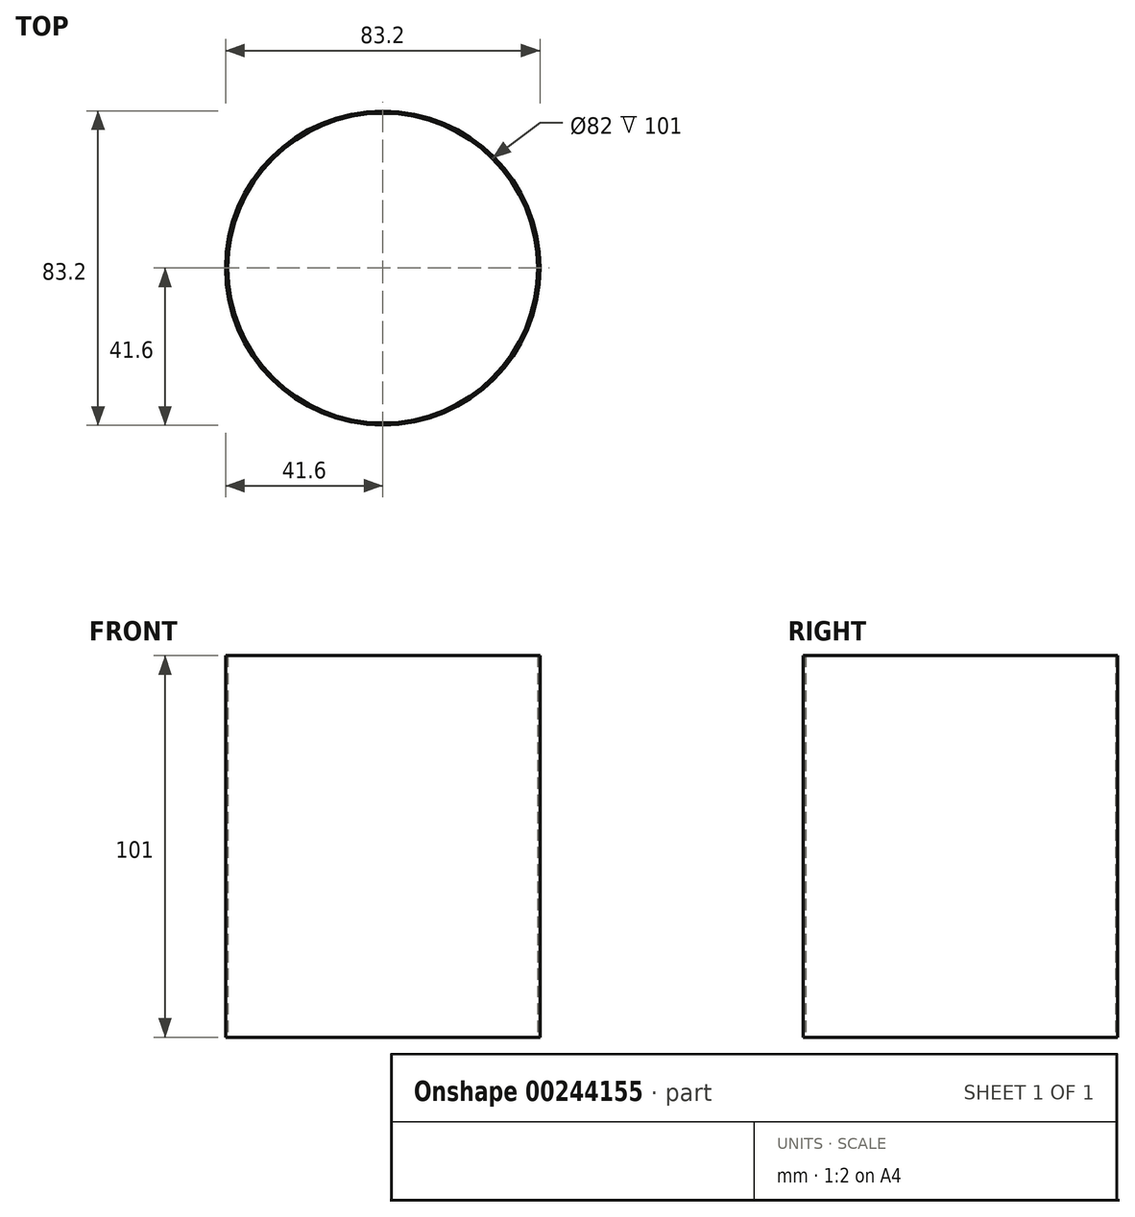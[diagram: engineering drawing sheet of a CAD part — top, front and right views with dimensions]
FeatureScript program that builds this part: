
annotation { "Feature Type Name" : "Feature", "Feature Type Description" : "" }
export const myFeature = defineFeature(function(context is Context, id is Id, definition is map)
    precondition{}
    {
        {
            var Q0;
            Q0=qCreatedBy(makeId("Top.planeOp"),FACE);
            var sketch = newSketch(context, id + "F0", { "sketchPlane" : qUnion([Q0])});
            skCircle(sketch, "E0", {"center": v(0, 0) * mm, "radius": 41 * mm});
            skCircle(sketch, "E1.0", {"center": v(0, 0) * mm, "radius": 41.6 * mm});
            skSolve(sketch);
        }
        {
            var Q0;
            Q0 = qSketchRegion(id + "F0", true);
            extrude(context, id + "F1", {"entities" : qUnion([Q0]), "depth" : 101 * mm});
        }
    });
